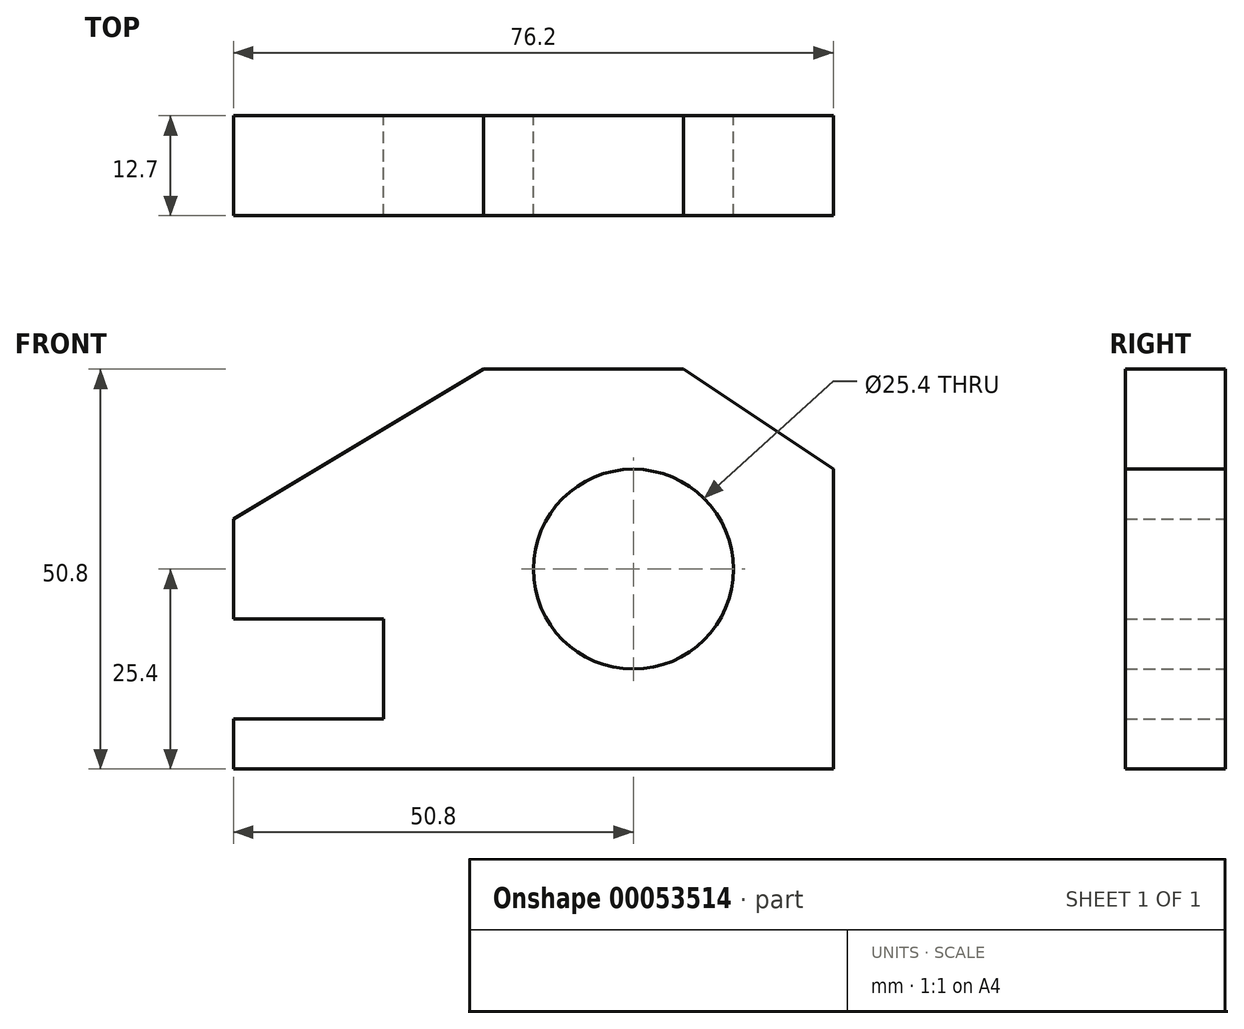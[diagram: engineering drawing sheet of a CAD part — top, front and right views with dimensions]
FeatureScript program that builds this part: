
annotation { "Feature Type Name" : "Feature", "Feature Type Description" : "" }
export const myFeature = defineFeature(function(context is Context, id is Id, definition is map)
    precondition{}
    {
        {
            var Q0;
            Q0=qCreatedBy(makeId("Front.planeOp"),FACE);
            var sketch = newSketch(context, id + "F0", { "sketchPlane" : qUnion([Q0])});
            skCircle(sketch, "E0", {"center": v(0, 0) * mm, "radius": 12.7 * mm});
            skLineSegment(sketch, "E1", {"start": v(6.35, 25.4) * mm, "end": v(-19.05, 25.4) * mm});
            skLineSegment(sketch, "E2", {"start": v(-19.05, 25.4) * mm, "end": v(-50.8, 6.35) * mm});
            skLineSegment(sketch, "E3", {"start": v(-50.8, 6.35) * mm, "end": v(-50.8, -6.35) * mm});
            skLineSegment(sketch, "E4", {"start": v(-50.8, -6.35) * mm, "end": v(-31.75, -6.35) * mm});
            skLineSegment(sketch, "E5", {"start": v(-31.75, -6.35) * mm, "end": v(-31.75, -19.05) * mm});
            skLineSegment(sketch, "E6", {"start": v(-31.75, -19.05) * mm, "end": v(-50.8, -19.05) * mm});
            skLineSegment(sketch, "E7", {"start": v(-50.8, -19.05) * mm, "end": v(-50.8, -25.4) * mm});
            skLineSegment(sketch, "E8", {"start": v(-50.8, -25.4) * mm, "end": v(25.4, -25.4) * mm});
            skLineSegment(sketch, "E9", {"start": v(25.4, -25.4) * mm, "end": v(25.4, 12.7) * mm});
            skLineSegment(sketch, "E10", {"start": v(25.4, 12.7) * mm, "end": v(6.35, 25.4) * mm});
            skSolve(sketch);
        }
        {
            var Q0;
            Q0 = qSketchRegion(id + "F0", true);
            extrude(context, id + "F1", {"entities" : qUnion([Q0]), "depth" : 12.7 * mm});
        }
    });
